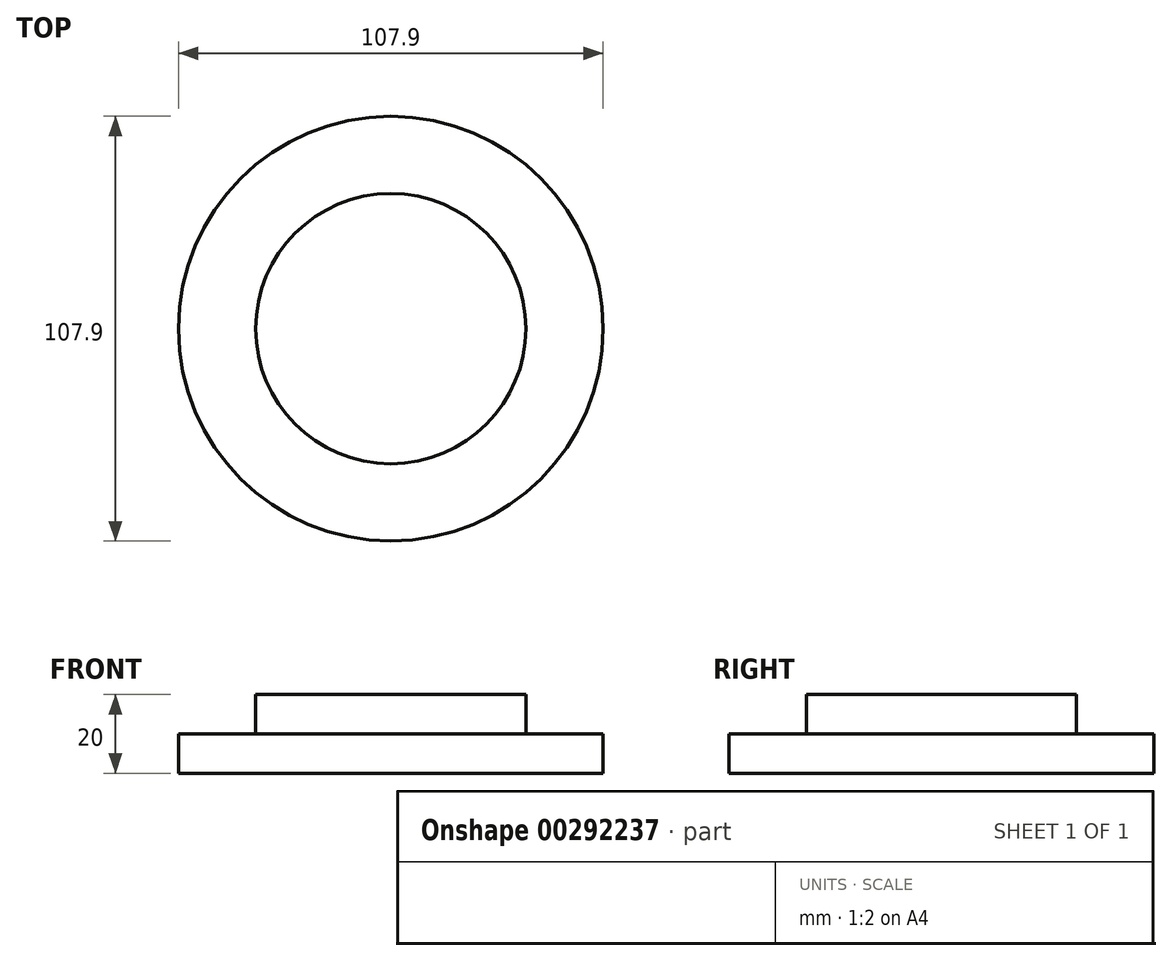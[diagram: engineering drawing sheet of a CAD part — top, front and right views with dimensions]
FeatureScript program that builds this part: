
annotation { "Feature Type Name" : "Feature", "Feature Type Description" : "" }
export const myFeature = defineFeature(function(context is Context, id is Id, definition is map)
    precondition{}
    {
        {
            var Q0;
            Q0=qCreatedBy(makeId("Top.planeOp"),FACE);
            var sketch = newSketch(context, id + "F0", { "sketchPlane" : qUnion([Q0])});
            skCircle(sketch, "E0", {"center": v(0, 0) * mm, "radius": 34.32 * mm});
            skSolve(sketch);
        }
        {
            var Q0;
            Q0 = qSketchRegion(id + "F0", true);
            extrude(context, id + "F1", {"entities" : qUnion([Q0]), "depth" : 20 * mm});
        }
        {
            var Q0;
            Q0=qCreatedBy(makeId("Top.planeOp"),FACE);
            var sketch = newSketch(context, id + "F2", { "sketchPlane" : qUnion([Q0])});
            skCircle(sketch, "E1", {"center": v(0, 0) * mm, "radius": 53.95 * mm});
            skSolve(sketch);
        }
        {
            var Q0;
            Q0 = qSketchRegion(id + "F2", true);
            extrude(context, id + "F3", {"entities" : qUnion([Q0]), "operationType" : NewBodyOperationType.ADD, "depth" : 10 * mm});
        }
        {
            var Q0;
            Q0=qCreatedBy(makeId("Top.planeOp"),FACE);
            var sketch = newSketch(context, id + "F4", { "sketchPlane" : qUnion([Q0])});
            skCircle(sketch, "E2", {"center": v(0, 0) * mm, "radius": 45.74 * mm});
            skSolve(sketch);
        }
        {
            var Q0;
            Q0 = qSketchRegion(id + "F4", true);
            extrude(context, id + "F5", {"entities" : qUnion([Q0]), "operationType" : NewBodyOperationType.ADD, "depth" : 10 * mm});
        }
    });
